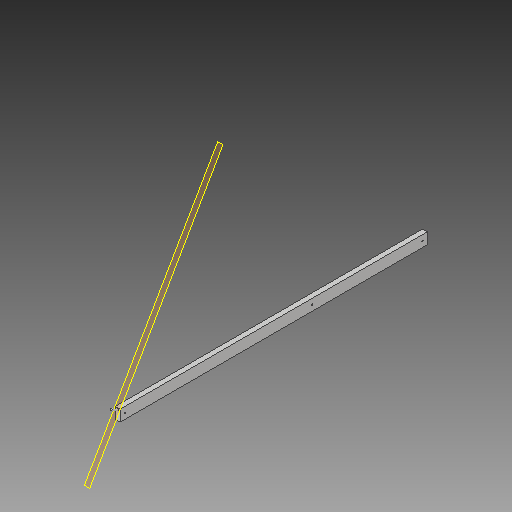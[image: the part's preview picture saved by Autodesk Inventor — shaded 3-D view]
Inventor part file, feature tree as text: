
AUTODESK INVENTOR PART (.ipt)
format: ipt  version: 2019 (Build 230136000, 136)  size: 126,976 bytes
history: native  units: in
note: dims shown in document units (in); Inventor stores cm internally (conversion verified against a paired STEP export)
features: extrude x5, sketch x5, plane x1
ambient origin geometry x8: Origin, YZ Plane, XZ Plane, XY Plane, X Axis, Y Axis, Z Axis, Center Point
bodies: Solid1 (feature_tree)
feature tree (11):
  extrude  "Extrusion1"  Depth=96.0in
  extrude  "Extrusion2"  Depth=1.5in
  extrude  "Extrusion15"  Depth=1.5in TaperAngle=0.0deg
  plane  "Work Plane9"
  extrude  "Extrusion16"  Depth=0.5in
  extrude  "Extrusion17"  Depth=1.5in
  sketch  "Sketch1"  dims[d0=3.5in d1=96.0in]
  sketch  "Sketch2"  dims[d2=3.5in d3=1.5in]
  sketch  "Sketch17"  dims[d4=0.5in d5=1.5in d6=0.0in]
  sketch  "Sketch18"  dims[d7=34.5in d8=0.5in]
  sketch  "Sketch19"  dims[d9=1.5in d10=0.0in d71=0.5in d72=1.5in d73=2.0in d74=0.0in d75=0.5in d76=2.0in d77=0.0in d78=1.0in d79=0.0in]
